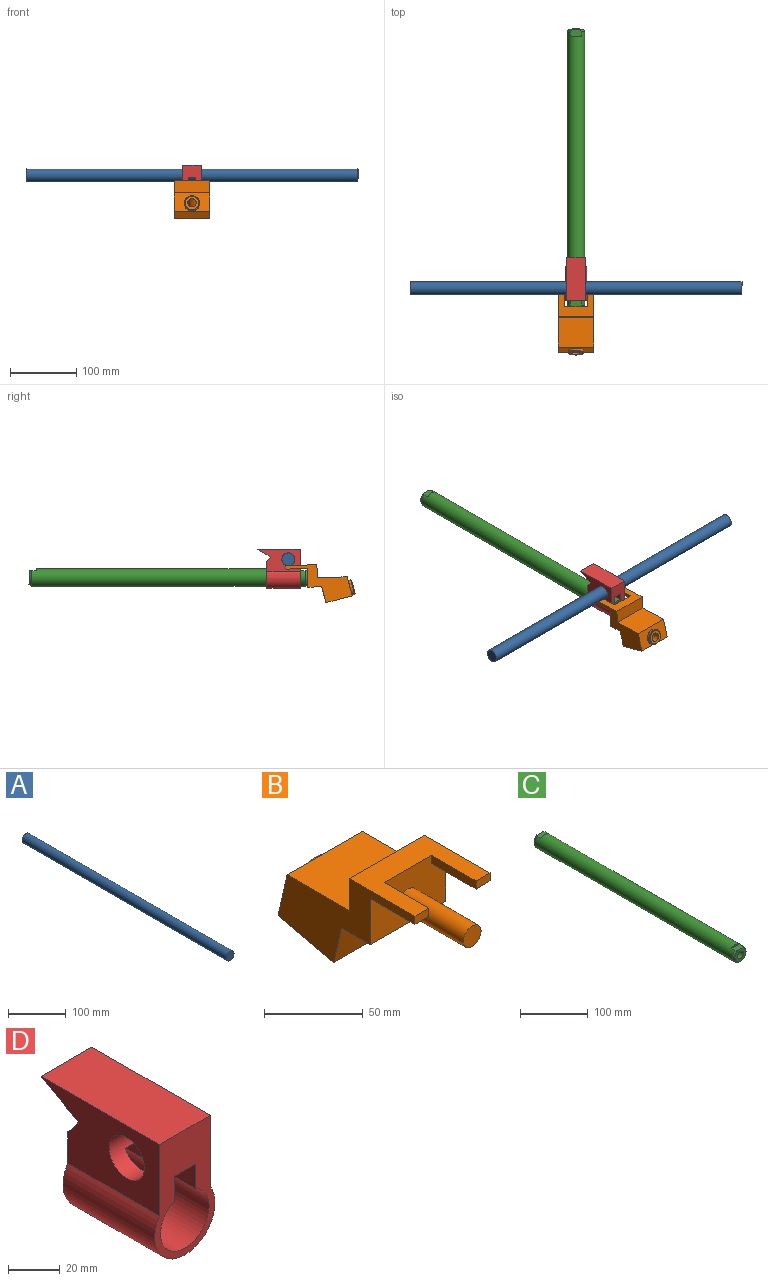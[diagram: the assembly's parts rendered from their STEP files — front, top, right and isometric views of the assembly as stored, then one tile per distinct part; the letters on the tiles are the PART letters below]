
ASSEMBLY  parts=4 mates=3
PART A: 3 faces, bbox 19.3x500x19.3 mm
  f0: cylinder r=9.65mm len=500mm, axis (0,1,0), area 30316.4mm2, adj f1,f2
  f1: plane 19.3x19.3mm, normal (0,-1,0), area 292.6mm2, adj f0
  f2: plane 19.3x19.3mm, normal (0,1,0), area 292.6mm2, adj f0
PART B: 22 faces, bbox 53.7x116.6x57.9 mm
  f0: plane 53.7x39.88mm, normal (0,0.22,-0.98), area 2196.3mm2, adj f2,f3,f12,f19
  f1: plane 20.76x20.24mm, normal (0,0.98,0.22), area 210.6mm2, adj f18,f21
  f2: plane 98.06x57.87mm, normal (-1,0,0), area 2114.8mm2, adj f0,f4,f5,f7,f8,f10,f11,f12
  f3: plane 98.06x57.87mm, normal (1,0,0), area 2114.8mm2, adj f0,f4,f5,f6,f9,f10,f11,f12
  f4: plane 53.7x44.87mm, normal (0,0,1), area 2409.7mm2, adj f2,f3,f17,f19
  f5: plane 53.7x46.64mm, normal (0,0,1), area 1433mm2, adj f2,f3,f6,f8,f10,f15,f16,f17
  f6: plane 10x5mm, normal (0,-1,0), area 50mm2, adj f3,f5,f9,f16
  f7: plane 31.8x10mm, normal (0,0,-1), area 318mm2, adj f2,f8,f10,f15
  f8: plane 10x5mm, normal (0,-1,0), area 50mm2, adj f2,f5,f7,f15
  f9: plane 31.8x10mm, normal (0,0,-1), area 318mm2, adj f3,f6,f10,f16
  f10: plane 53.7x33.49mm, normal (0,-1,0), area 1570.7mm2, adj f2,f3,f5,f7,f9,f11,f13,f15
  f11: plane 53.7x20.84mm, normal (0,0,-1), area 1119mm2, adj f2,f3,f10,f12
  f12: plane 53.7x24.38mm, normal (0,-0.98,-0.22), area 1214.6mm2, adj f0,f2,f3,f11,f18
  f13: cylinder r=6.38mm len=45.9mm, axis (0,1,0), area 1840mm2, adj f10,f14
  f14: plane 12.76x12.76mm, normal (0,-1,0), area 127.9mm2, adj f13
  f15: plane 31.8x5mm, normal (1,0,0), area 159mm2, adj f5,f7,f8,f10
  f16: plane 31.8x5mm, normal (-1,0,0), area 159mm2, adj f5,f6,f9,f10
  f17: plane 53.7x20mm, normal (0,1,0), area 1074mm2, adj f2,f3,f4,f5
  f18: cylinder r=6.38mm len=47.59mm, axis (0,0.98,0.22), area 1840mm2, adj f1,f12
  f19: plane 53.7x28.81mm, normal (0,0.98,0.22), area 1179.7mm2, adj f0,f2,f3,f4,f20
  f20: cylinder r=11.38mm len=23.08mm, axis (0,0.98,0.22), area 286mm2, adj f19,f21
  f21: cone r=10.38mm half-angle=45deg, axis (0,-0.98,-0.22), area 96.7mm2, adj f1,f20
PART C: 10 faces, bbox 26.5x419.9x26.5 mm
  f0: plane 16.8x10.62mm, normal (0,0,1), area 170mm2, adj f2,f3,f4,f5
  f1: cylinder r=6.25mm len=419.47mm, axis (0,-1,0), area 16454.3mm2, adj f5,f9
  f2: cone r=13.25mm half-angle=26.6deg, axis (0,1,0), area 251.9mm2, adj f0,f3,f5
  f3: cylinder r=13.25mm len=412mm, axis (0,1,0), area 34027.1mm2, adj f0,f2,f4,f6,f7,f8
  f4: plane 16.79x3mm, normal (0,-1,0), area 34.4mm2, adj f0,f3
  f5: plane 23x21.54mm, normal (0,-1,0.04), area 281.9mm2, adj f0,f1,f2
  f6: plane 16.8x10.62mm, normal (0,0,1), area 170mm2, adj f3,f7,f8,f9
  f7: cone r=13.25mm half-angle=26.6deg, axis (0,-1,0), area 251.9mm2, adj f3,f6,f9
  f8: plane 16.79x3mm, normal (0,1,0), area 34.4mm2, adj f3,f6
  f9: plane 23x21.54mm, normal (0,1,0.04), area 281.9mm2, adj f1,f6,f7
PART D: 15 faces, bbox 32.9x64.6x59 mm
  f0: plane 40x32.9mm, normal (0,1,0), area 431.4mm2, adj f1,f3,f5,f6,f8,f11,f14
  f1: cylinder r=13.25mm len=50mm, axis (0,1,0), area 3556.7mm2, adj f0,f7,f11,f14
  f2: cylinder r=9.65mm len=27.7mm, axis (-1,0,0), area 1417.5mm2, adj f3,f5,f11,f12,f13,f14
  f3: plane 64.6x33.67mm, normal (1,0,0), area 1418.5mm2, adj f0,f2,f4,f6,f7,f8,f9,f10
  f4: plane 64.6x27.7mm, normal (0,0,1), area 1789.4mm2, adj f3,f5,f7,f10
  f5: plane 64.6x33.67mm, normal (-1,0,0), area 1418.5mm2, adj f0,f2,f4,f6,f7,f8,f9,f10
  f6: cylinder r=16.45mm len=50mm, axis (0,1,0), area 3521.5mm2, adj f0,f3,f5,f7
  f7: plane 59x32.9mm, normal (0,-1,0), area 957.7mm2, adj f1,f3,f4,f5,f6,f11,f12,f14
  f8: plane 27.7x7.21mm, normal (0,0.77,0.64), area 259.8mm2, adj f0,f3,f5,f9,f13
  f9: plane 27.7x6mm, normal (0,0.52,-0.86), area 193.9mm2, adj f3,f5,f8,f10
  f10: plane 27.7x14.6mm, normal (0,0.49,-0.87), area 463.7mm2, adj f3,f4,f5,f9
  f11: plane 50x11.66mm, normal (1,0,0), area 509.1mm2, adj f0,f1,f2,f7,f12,f13
  f12: plane 11.7x9mm, normal (0,0,-1), area 105.3mm2, adj f2,f7,f11,f14
  f13: plane 23.3x11.7mm, normal (0,0,-1), area 272.6mm2, adj f2,f8,f11,f14
  f14: plane 50x11.66mm, normal (-1,0,0), area 509.1mm2, adj f0,f1,f2,f7,f12,f13
PLACE A rot(axis=(0,0,1),90deg) t=(-281.04,-152.36,96.72)mm
PLACE B rot(axis=(0,-0.02,-1),180deg) t=(-31.04,-180.97,75.69)mm
PLACE C t=(-31.04,28.29,69.32)mm fixed
PLACE D rot(axis=(0.87,0.47,-0.18),0deg) t=(-31.04,-120.21,69.32)mm
MATE fastened C.f3 <-> D.f1  axis (0,1,0) through (-31.04,28.29,69.32)mm
MATE fastened A.f0 <-> D.f2  axis (-1,0,0) through (-31.04,-152.36,96.72)mm
MATE fastened B.f13 <-> C.f5  axis (0,1,-0.04) through (-31.04,-181.21,69.32)mm
